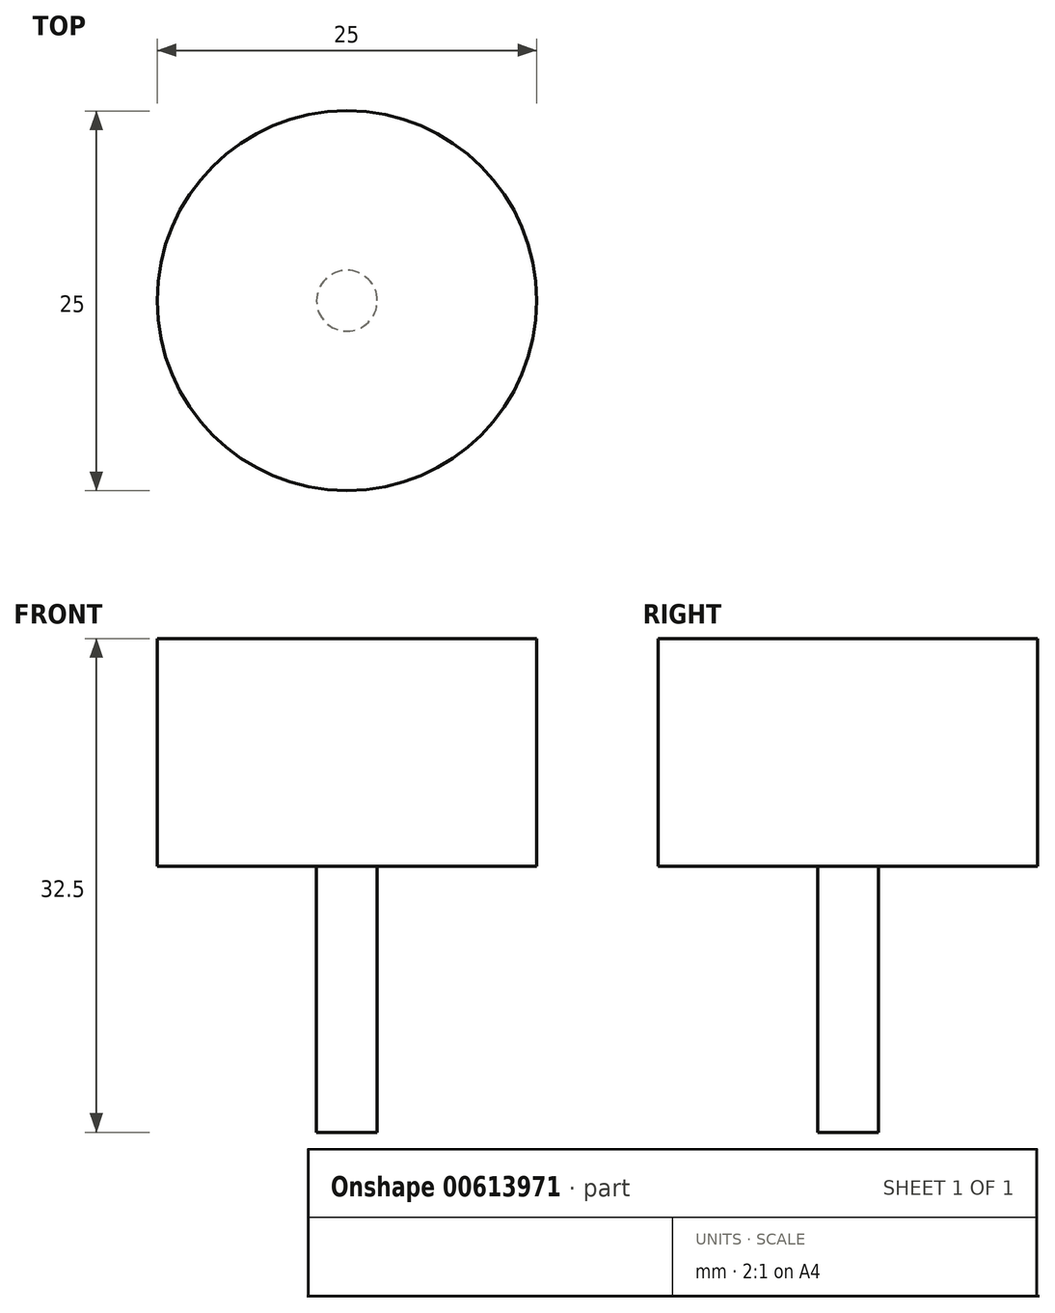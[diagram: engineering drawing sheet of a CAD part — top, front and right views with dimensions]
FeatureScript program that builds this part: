
annotation { "Feature Type Name" : "Feature", "Feature Type Description" : "" }
export const myFeature = defineFeature(function(context is Context, id is Id, definition is map)
    precondition{}
    {
        {
            var Q0;
            Q0=qCreatedBy(makeId("Top.planeOp"),FACE);
            var sketch = newSketch(context, id + "F0", { "sketchPlane" : qUnion([Q0])});
            skCircle(sketch, "E0", {"center": v(-42.35, 7.08) * mm, "radius": 2 * mm});
            skSolve(sketch);
        }
        {
            var Q0;
            Q0 = qSketchRegion(id + "F0", true);
            extrude(context, id + "F1", {"entities" : qUnion([Q0]), "depth" : 25 * mm, "offsetDistance" : 25 * mm});
        }
        {
            var Q0;
            Q0=makeQuery(id+"F1.opExtrude","CAP_FACE",FACE,{"disambiguationData":[OSD([sQuery(id+"F0.wireOp",EDGE,"E0")])],"isStart":false});
            var sketch = newSketch(context, id + "F2", { "sketchPlane" : qUnion([Q0])});
            skCircle(sketch, "E1", {"center": v(-42.35, 7.08) * mm, "radius": 12.5 * mm});
            skSolve(sketch);
        }
        {
            var Q0;
            Q0 = qSketchRegion(id + "F2", true);
            extrude(context, id + "F3", {"entities" : qUnion([Q0]), "operationType" : NewBodyOperationType.ADD, "endBound" : BoundingType.SYMMETRIC, "depth" : 15 * mm, "offsetDistance" : 25 * mm});
        }
    });
